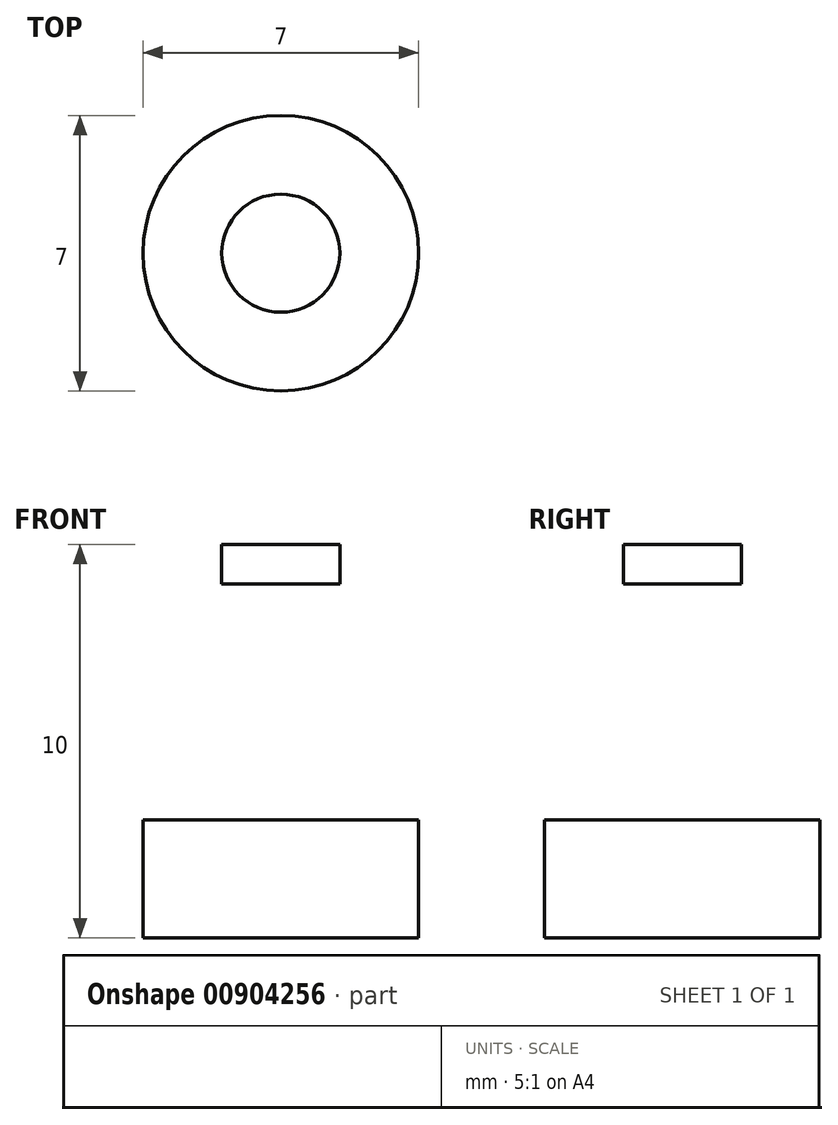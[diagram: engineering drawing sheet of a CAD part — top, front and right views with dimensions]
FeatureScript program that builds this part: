
annotation { "Feature Type Name" : "Feature", "Feature Type Description" : "" }
export const myFeature = defineFeature(function(context is Context, id is Id, definition is map)
    precondition{}
    {
        {
            var Q0;
            Q0=qCreatedBy(makeId("Front.planeOp"),FACE);
            var sketch = newSketch(context, id + "F0", { "sketchPlane" : qUnion([Q0])});
            skLineSegment(sketch, "E0.bottom", {"start": v(0, 0) * mm, "end": v(-3.5, 0) * mm});
            skLineSegment(sketch, "E0.top", {"start": v(0, 3) * mm, "end": v(-3.5, 3) * mm});
            skLineSegment(sketch, "E0.left", {"start": v(0, 0) * mm, "end": v(0, 3) * mm});
            skLineSegment(sketch, "E0.right", {"start": v(-3.5, 0) * mm, "end": v(-3.5, 3) * mm});
            skLineSegment(sketch, "E1.bottom", {"start": v(0, 3) * mm, "end": v(-1, 3) * mm});
            skLineSegment(sketch, "E1.top", {"start": v(0, 9) * mm, "end": v(-1, 9) * mm});
            skLineSegment(sketch, "E1.left", {"start": v(0, 3) * mm, "end": v(0, 9) * mm});
            skLineSegment(sketch, "E1.right", {"start": v(-1, 3) * mm, "end": v(-1, 9) * mm});
            skLineSegment(sketch, "E2.bottom", {"start": v(0, 9) * mm, "end": v(-1.5, 9) * mm});
            skLineSegment(sketch, "E2.top", {"start": v(0, 10) * mm, "end": v(-1.5, 10) * mm});
            skLineSegment(sketch, "E2.left", {"start": v(0, 9) * mm, "end": v(0, 10) * mm});
            skLineSegment(sketch, "E2.right", {"start": v(-1.5, 9) * mm, "end": v(-1.5, 10) * mm});
            skSolve(sketch);
        }
        {
            var Q0;
            Q0=makeQuery(id+"F0.imprint","IMPRINT",FACE,{"disambiguationData":[TD([[makeQuery(id+"F0.imprint","IMPRINT",EDGE,{"derivedFrom":sQuery(id+"F0.wireOp",EDGE,"E0.bottom")}),-1.0]])]});
            var Q1;
            Q1=makeQuery(id+"F0.imprint","IMPRINT",FACE,{"disambiguationData":[TD([[makeQuery(id+"F0.imprint","IMPRINT",EDGE,{"derivedFrom":sQuery(id+"F0.wireOp",EDGE,"E1.bottom")}),-1.0]])]});
            var Q2;
            Q2=makeQuery(id+"F0.imprint","IMPRINT",FACE,{"disambiguationData":[TD([[makeQuery(id+"F0.imprint","IMPRINT",EDGE,{"derivedFrom":sQuery(id+"F0.wireOp",EDGE,"E2.top")}),1.0]])]});
            var Q3;
            Q3=sQuery(id+"F0.wireOp",EDGE,"E1.left");
            revolve(context, id + "F1", {"surfaceOperationType" : NewSurfaceOperationType.NEW, "entities" : qUnion([Q0, Q1, Q2]), "axis" : qUnion([Q3]), "revolveType" : RevolveType.FULL});
        }
    });
